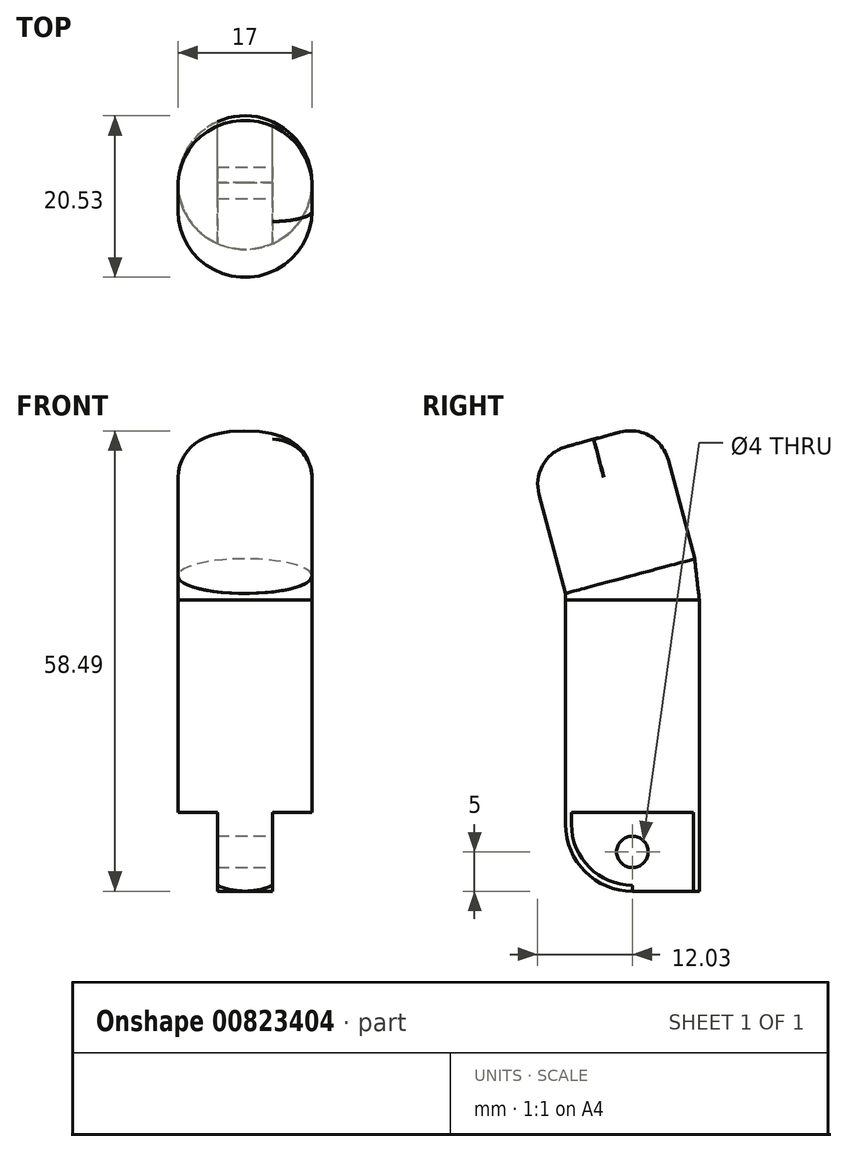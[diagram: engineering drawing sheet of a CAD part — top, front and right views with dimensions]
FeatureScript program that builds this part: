
annotation { "Feature Type Name" : "Feature", "Feature Type Description" : "" }
export const myFeature = defineFeature(function(context is Context, id is Id, definition is map)
    precondition{}
    {
        {
            var Q0;
            Q0=qCreatedBy(makeId("Top.planeOp"),FACE);
            var sketch = newSketch(context, id + "F0", { "sketchPlane" : qUnion([Q0])});
            skCircle(sketch, "E0", {"center": v(0, 0) * mm, "radius": 8.5 * mm});
            skSolve(sketch);
        }
        {
            var Q0;
            Q0 = qSketchRegion(id + "F0", true);
            extrude(context, id + "F1", {"entities" : qUnion([Q0]), "endBound" : BoundingType.SYMMETRIC, "depth" : 37 * mm, "offsetDistance" : 25 * mm});
        }
        {
            var Q0;
            Q0=makeQuery(id+"F1.opExtrude","CAP_FACE",FACE,{"disambiguationData":[OSD([sQuery(id+"F0.wireOp",EDGE,"E0")])],"isStart":true});
            fillet(context, id + "F2", {"entities" : qUnion([Q0]), "radius" : 8.5 * mm, "tangentPropagation" : true, "allowEdgeOverflow" : false});
        }
        {
            var Q0;
            Q0=qCreatedBy(makeId("Top.planeOp"),FACE);
            cPlane(context, id + "F3", {"entities" : qUnion([Q0]), "cplaneType" : CPlaneType.OFFSET, "offset" : 18.5 * mm, "oppositeDirection" : true, "width" : 150 * mm, "height" : 150 * mm});
        }
        {
            var Q0;
            Q0=qCreatedBy(id+"F3.planeOp",FACE);
            var sketch = newSketch(context, id + "F4", { "sketchPlane" : qUnion([Q0])});
            skLineSegment(sketch, "E1.bottom", {"start": v(3.5, -15.65) * mm, "end": v(-3.5, -15.65) * mm});
            skLineSegment(sketch, "E1.top", {"start": v(3.5, 15.65) * mm, "end": v(-3.5, 15.65) * mm});
            skLineSegment(sketch, "E1.left", {"start": v(3.5, -15.65) * mm, "end": v(3.5, 15.65) * mm});
            skLineSegment(sketch, "E1.right", {"start": v(-3.5, -15.65) * mm, "end": v(-3.5, 15.65) * mm});
            skPoint(sketch, "E1.middle", {"position": v(0, 0) * mm});
            skLineSegment(sketch, "E2.bottom", {"start": v(11.48, -19.87) * mm, "end": v(-11.48, -19.87) * mm});
            skLineSegment(sketch, "E2.top", {"start": v(11.48, 19.87) * mm, "end": v(-11.48, 19.87) * mm});
            skLineSegment(sketch, "E2.left", {"start": v(11.48, -19.87) * mm, "end": v(11.48, 19.87) * mm});
            skLineSegment(sketch, "E2.right", {"start": v(-11.48, -19.87) * mm, "end": v(-11.48, 19.87) * mm});
            skSolve(sketch);
        }
        {
            var Q0;
            Q0 = qSketchRegion(id + "F4", true);
            extrude(context, id + "F5", {"entities" : qUnion([Q0]), "operationType" : NewBodyOperationType.REMOVE, "depth" : 10 * mm, "offsetDistance" : 25 * mm});
        }
        {
            var Q0;
            Q0=qCreatedBy(id+"F3.planeOp",FACE);
            var sketch = newSketch(context, id + "F6", { "sketchPlane" : qUnion([Q0])});
            skLineSegment(sketch, "E3.bottom", {"start": v(3.5, 0) * mm, "end": v(-3.5, 0) * mm});
            skLineSegment(sketch, "E3.left", {"start": v(3.5, 0) * mm, "end": v(3.5, 7.75) * mm});
            skLineSegment(sketch, "E3.right", {"start": v(-3.5, 0) * mm, "end": v(-3.5, 7.75) * mm});
            skArc(sketch, "E4", {"start": v(3.5, 7.75) * mm, "mid": v(0, 8.5) * mm, "end": v(-3.5, 7.75) * mm});
            skSolve(sketch);
        }
        {
            var Q0;
            Q0 = qSketchRegion(id + "F6", true);
            extrude(context, id + "F7", {"entities" : qUnion([Q0]), "operationType" : NewBodyOperationType.ADD, "depth" : 10 * mm, "offsetDistance" : 25 * mm});
        }
        {
            var Q0;
            Q0=qCreatedBy(makeId("Right.planeOp"),FACE);
            var sketch = newSketch(context, id + "F8", { "sketchPlane" : qUnion([Q0])});
            skLineSegment(sketch, "E5", {"start": v(0, 18.5) * mm, "end": v(31.47, 26.93) * mm});
            skSolve(sketch);
        }
        {
            var Q0;
            Q0 = qBodyType(qCreatedBy(id + "F8" ,EDGE), BodyType.WIRE);
            cPlane(context, id + "F9", {"entities" : qUnion([Q0]), "cplaneType" : CPlaneType.LINE_ANGLE, "offset" : 25 * mm, "angle" : 0 * degree, "width" : 150 * mm, "height" : 150 * mm});
        }
        {
            var Q0;
            Q0=qCreatedBy(id+"F9.planeOp",FACE);
            cPlane(context, id + "F10", {"entities" : qUnion([Q0]), "cplaneType" : CPlaneType.OFFSET, "offset" : 3 * mm, "width" : 150 * mm, "height" : 150 * mm});
        }
        {
            var Q0;
            Q0=qCreatedBy(id+"F10.planeOp",FACE);
            var sketch = newSketch(context, id + "F11", { "sketchPlane" : qUnion([Q0])});
            skCircle(sketch, "E6", {"center": v(0, 5.28) * mm, "radius": 8.5 * mm});
            skSolve(sketch);
        }
        {
            var Q0;
            Q0=makeQuery(id+"F1.opExtrude","CAP_FACE",FACE,{"disambiguationData":[OSD([sQuery(id+"F0.wireOp",EDGE,"E0")])],"isStart":false});
            var Q1;
            Q1=makeQuery(id+"F11.imprint","IMPRINT",FACE,{"disambiguationData":[TD([[makeQuery(id+"F11.imprint","IMPRINT",EDGE,{"derivedFrom":sQuery(id+"F11.wireOp",EDGE,"E6")}),1.0]])]});
            loft(context, id + "F12", {"operationType" : NewBodyOperationType.ADD, "sheetProfilesArray" : [{ "sheetProfileEntities" : qUnion([Q0]) }, { "sheetProfileEntities" : qUnion([Q1]) }]});
        }
        {
            var Q0;
            Q0=makeQuery(id+"F12.opLoft","CAP_FACE",FACE,{"disambiguationData":[OSD([makeQuery(id+"F11.imprint","IMPRINT",FACE,{"disambiguationData":[TD([[makeQuery(id+"F11.imprint","IMPRINT",EDGE,{"derivedFrom":sQuery(id+"F11.wireOp",EDGE,"E6")}),1.0]])]})])],"isStart":true});
            var sketch = newSketch(context, id + "F13", { "sketchPlane" : qUnion([Q0])});
            skCircle(sketch, "E7", {"center": v(0, 5.3) * mm, "radius": 8.5 * mm});
            skSolve(sketch);
        }
        {
            var Q0;
            Q0 = qSketchRegion(id + "F13", true);
            extrude(context, id + "F14", {"entities" : qUnion([Q0]), "operationType" : NewBodyOperationType.ADD, "depth" : 18 * mm, "offsetDistance" : 25 * mm});
        }
        {
            var Q0;
            Q0=makeQuery(id+"F14.opExtrude","CAP_FACE",FACE,{"disambiguationData":[OSD([sQuery(id+"F13.wireOp",EDGE,"E7")])],"isStart":false});
            fillet(context, id + "F15", {"entities" : qUnion([Q0]), "radius" : 5 * mm, "tangentPropagation" : true, "allowEdgeOverflow" : false});
        }
        {
            var Q0;
            Q0=qCreatedBy(makeId("Right.planeOp"),FACE);
            var sketch = newSketch(context, id + "F16", { "sketchPlane" : qUnion([Q0])});
            skCircle(sketch, "E8", {"center": v(0, -13.5) * mm, "radius": 2 * mm});
            skSolve(sketch);
        }
        {
            var Q0;
            Q0 = qSketchRegion(id + "F16", true);
            extrude(context, id + "F17", {"entities" : qUnion([Q0]), "operationType" : NewBodyOperationType.REMOVE, "endBound" : BoundingType.SYMMETRIC, "oppositeDirection" : true, "depth" : 25 * mm, "offsetDistance" : 25 * mm});
        }
    });
